# Revit family: Sanitary_Taps-Mixers_hansgrohe_73021USA-Tecturis-E-Single-lever-basin-m__
name_source: partatom
category: Plumbing Fixtures
revit_build: Autodesk Revit 2018 (Build: 20170223_1515(x64)
units: mm (PartAtom-declared; Revit-internal decimal feet)

## family parameters
Always vertical = No
Cut with Voids When Loaded = No
OmniClass Number = 23.31.11.00
OmniClass Title = Faucets
Part Type = Normal
Room Calculation Point = No
Round Connector Dimension = Use Diameter
Shared = No
Work Plane-Based = Yes

## types (3) — shared parameters
Always visible = Yes
BIMobject category = Taps & Mixers
Connector Description = Water Inlet 3/8
Default Elevation = 4' - 0"
Description = Tecturis E Single lever basin mixer 110 Fine CoolStart without waste set
Design country = Germany
Diameter = 0"
EAN code = 4059625473788
Edition number = 1
GTIN code = https://4059625473788
IFC Classification = Valve
Manufacturer = Hansgrohe
Manufacturer country = Germany
Manufacturer name = hansgrohe
Masterformat 2014 Code = 22 41 39
Masterformat 2014 Description = Residential Faucets, Supplies, and Trim
Model = 73021USA
OmniClass Code = 23-31 11 00
OmniClass Description = Faucets
Product Guid = 07c8cb10-88af-4d8b-b5ab-8d18f23c1970
Product SKU = 73021USA
Product data url = https://bimobject.com
Product family = Tecturis E
Product group = Basin mixers
Product name = 73021USA Tecturis E Single lever basin mixer 110 Fine CoolStart without waste set
Product url = https://pro.hansgrohe.com
QR code = https://bimobject.com
UNSPSC Code = 3018
URL = https://www.hansgrohe.com
Uniclass 2015 Code = Pr_40_20_87
Uniclass 2015 Name = Taps and water supply outlet fittings
Uniformat II Code = D2010
Uniformat II Description = Plumbing Fixtures

## per-type parameters (varying)
| type | Material 1 |
| 671 Matte Black | Hansgrohe - Metal - 671 Matte Black |
| 821 Brushed Nickel | Hansgrohe - Metal - 821 Brushed Nickel |
| 001 Chrome | Hansgrohe - Metal - 001 Chrome |

## geometry (parser evidence)
native form markers: Sweep x2
no freeform markers — native parametric forms only
